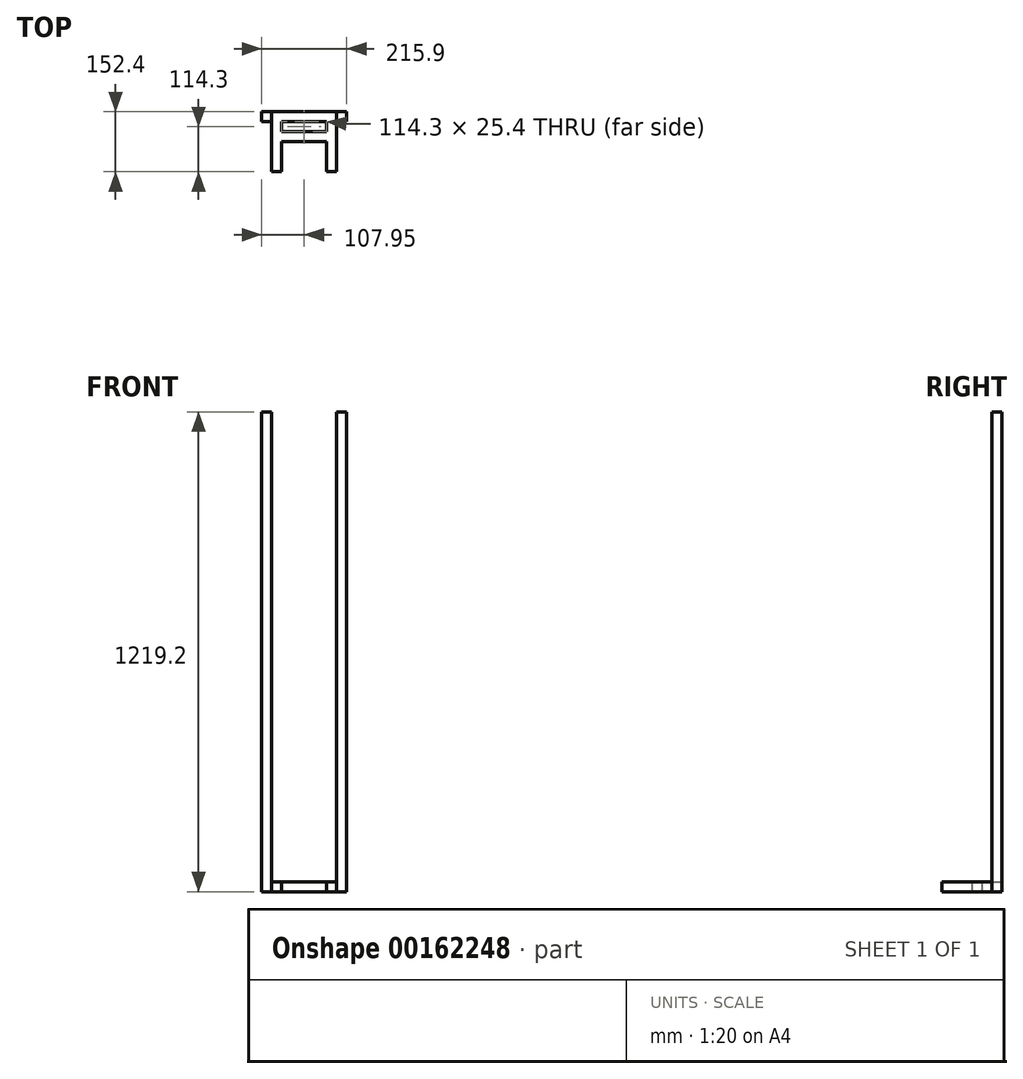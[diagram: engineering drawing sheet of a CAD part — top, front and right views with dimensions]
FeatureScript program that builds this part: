
annotation { "Feature Type Name" : "Feature", "Feature Type Description" : "" }
export const myFeature = defineFeature(function(context is Context, id is Id, definition is map)
    precondition{}
    {
        {
            var Q0;
            Q0=qCreatedBy(makeId("Front.planeOp"),FACE);
            var sketch = newSketch(context, id + "F0", { "sketchPlane" : qUnion([Q0])});
            skLineSegment(sketch, "E0.bottom", {"start": v(107.95, 609.6) * mm, "end": v(82.55, 609.6) * mm});
            skLineSegment(sketch, "E0.top", {"start": v(107.95, -609.6) * mm, "end": v(-107.95, -609.6) * mm});
            skLineSegment(sketch, "E0.left", {"start": v(107.95, 609.6) * mm, "end": v(107.95, -609.6) * mm});
            skLineSegment(sketch, "E0.right", {"start": v(-107.95, 609.6) * mm, "end": v(-107.95, -609.6) * mm});
            skPoint(sketch, "E0.middle", {"position": v(0, 0) * mm});
            skLineSegment(sketch, "E1.bottom", {"start": v(82.55, -584.2) * mm, "end": v(-82.55, -584.2) * mm});
            skLineSegment(sketch, "E1.left", {"start": v(82.55, -584.2) * mm, "end": v(82.55, 609.6) * mm});
            skLineSegment(sketch, "E1.right", {"start": v(-82.55, -584.2) * mm, "end": v(-82.55, 609.6) * mm});
            skLineSegment(sketch, "E2.top", {"start": v(-82.55, -609.6) * mm, "end": v(-107.95, -609.6) * mm});
            skLineSegment(sketch, "E2.right", {"start": v(-107.95, -584.2) * mm, "end": v(-107.95, -609.6) * mm});
            skLineSegment(sketch, "E3.top", {"start": v(82.55, -609.6) * mm, "end": v(107.95, -609.6) * mm});
            skLineSegment(sketch, "E3.right", {"start": v(107.95, -584.2) * mm, "end": v(107.95, -609.6) * mm});
            skLineSegment(sketch, "E4.trimOffspring", {"start": v(-82.55, 609.6) * mm, "end": v(-107.95, 609.6) * mm});
            skPoint(sketch, "E1.top.end.orphan", {"position": v(-82.55, 584.2) * mm});
            skPoint(sketch, "E1.top.start.orphan", {"position": v(82.55, 584.2) * mm});
            skSolve(sketch);
        }
        {
            var Q0;
            Q0=makeQuery(id+"F0.imprint","IMPRINT",FACE,{"disambiguationData":[TD([[makeQuery(id+"F0.imprint","IMPRINT",EDGE,{"derivedFrom":sQuery(id+"F0.wireOp",EDGE,"E0.bottom")}),1.0]])]});
            extrude(context, id + "F1", {"entities" : qUnion([Q0]), "depth" : 25.4 * mm});
        }
        {
            var Q0;
            Q0=makeQuery(id+"F1.opExtrude","CAP_FACE",FACE,{"disambiguationData":[OSD([sQuery(id+"F0.wireOp",EDGE,"E0.bottom"),sQuery(id+"F0.wireOp",EDGE,"E0.top"),sQuery(id+"F0.wireOp",EDGE,"E0.left"),sQuery(id+"F0.wireOp",EDGE,"E0.right"),sQuery(id+"F0.wireOp",EDGE,"E1.bottom"),sQuery(id+"F0.wireOp",EDGE,"E1.left"),sQuery(id+"F0.wireOp",EDGE,"E1.right"),sQuery(id+"F0.wireOp",EDGE,"E2.top"),sQuery(id+"F0.wireOp",EDGE,"E2.right"),sQuery(id+"F0.wireOp",EDGE,"E3.top"),sQuery(id+"F0.wireOp",EDGE,"E3.right"),sQuery(id+"F0.wireOp",EDGE,"E4.trimOffspring")])],"isStart":false});
            var sketch = newSketch(context, id + "F2", { "sketchPlane" : qUnion([Q0])});
            skLineSegment(sketch, "E5.bottom", {"start": v(-82.55, -584.2) * mm, "end": v(-57.15, -584.2) * mm});
            skLineSegment(sketch, "E5.top", {"start": v(-82.55, -609.6) * mm, "end": v(-57.15, -609.6) * mm});
            skLineSegment(sketch, "E5.left", {"start": v(-82.55, -584.2) * mm, "end": v(-82.55, -609.6) * mm});
            skLineSegment(sketch, "E5.right", {"start": v(-57.15, -584.2) * mm, "end": v(-57.15, -609.6) * mm});
            skLineSegment(sketch, "E6.bottom", {"start": v(82.55, -584.2) * mm, "end": v(57.15, -584.2) * mm});
            skLineSegment(sketch, "E6.top", {"start": v(82.55, -609.6) * mm, "end": v(57.15, -609.6) * mm});
            skLineSegment(sketch, "E6.left", {"start": v(82.55, -584.2) * mm, "end": v(82.55, -609.6) * mm});
            skLineSegment(sketch, "E6.right", {"start": v(57.15, -584.2) * mm, "end": v(57.15, -609.6) * mm});
            skSolve(sketch);
        }
        {
            var Q0;
            Q0=makeQuery(id+"F2.imprint","IMPRINT",FACE,{"disambiguationData":[TD([[makeQuery(id+"F2.imprint","IMPRINT",EDGE,{"derivedFrom":sQuery(id+"F2.wireOp",EDGE,"E5.bottom")}),1.0]])]});
            var Q1;
            Q1=makeQuery(id+"F2.imprint","IMPRINT",FACE,{"disambiguationData":[TD([[makeQuery(id+"F2.imprint","IMPRINT",EDGE,{"derivedFrom":sQuery(id+"F2.wireOp",EDGE,"E6.bottom")}),1.0]])]});
            extrude(context, id + "F3", {"entities" : qUnion([Q0, Q1]), "operationType" : NewBodyOperationType.ADD, "depth" : 127 * mm});
        }
        {
            var Q0;
            Q0=makeQuery(id+"F3.opExtrude","SWEPT_FACE",FACE,{"disambiguationData":[OSD([sQuery(id+"F2.wireOp",EDGE,"E5.right")])]});
            var sketch = newSketch(context, id + "F4", { "sketchPlane" : qUnion([Q0])});
            skLineSegment(sketch, "E7.bottom", {"start": v(-50.8, -584.2) * mm, "end": v(-76.2, -584.2) * mm});
            skLineSegment(sketch, "E7.top", {"start": v(-50.8, -609.6) * mm, "end": v(-76.2, -609.6) * mm});
            skLineSegment(sketch, "E7.left", {"start": v(-50.8, -584.2) * mm, "end": v(-50.8, -609.6) * mm});
            skLineSegment(sketch, "E7.right", {"start": v(-76.2, -584.2) * mm, "end": v(-76.2, -609.6) * mm});
            skSolve(sketch);
        }
        {
            var Q0;
            Q0=makeQuery(id+"F4.imprint","IMPRINT",FACE,{"disambiguationData":[TD([[makeQuery(id+"F4.imprint","IMPRINT",EDGE,{"derivedFrom":sQuery(id+"F4.wireOp",EDGE,"E7.bottom")}),-1.0]])]});
            extrude(context, id + "F5", {"entities" : qUnion([Q0]), "operationType" : NewBodyOperationType.ADD, "depth" : 114.3 * mm});
        }
    });
